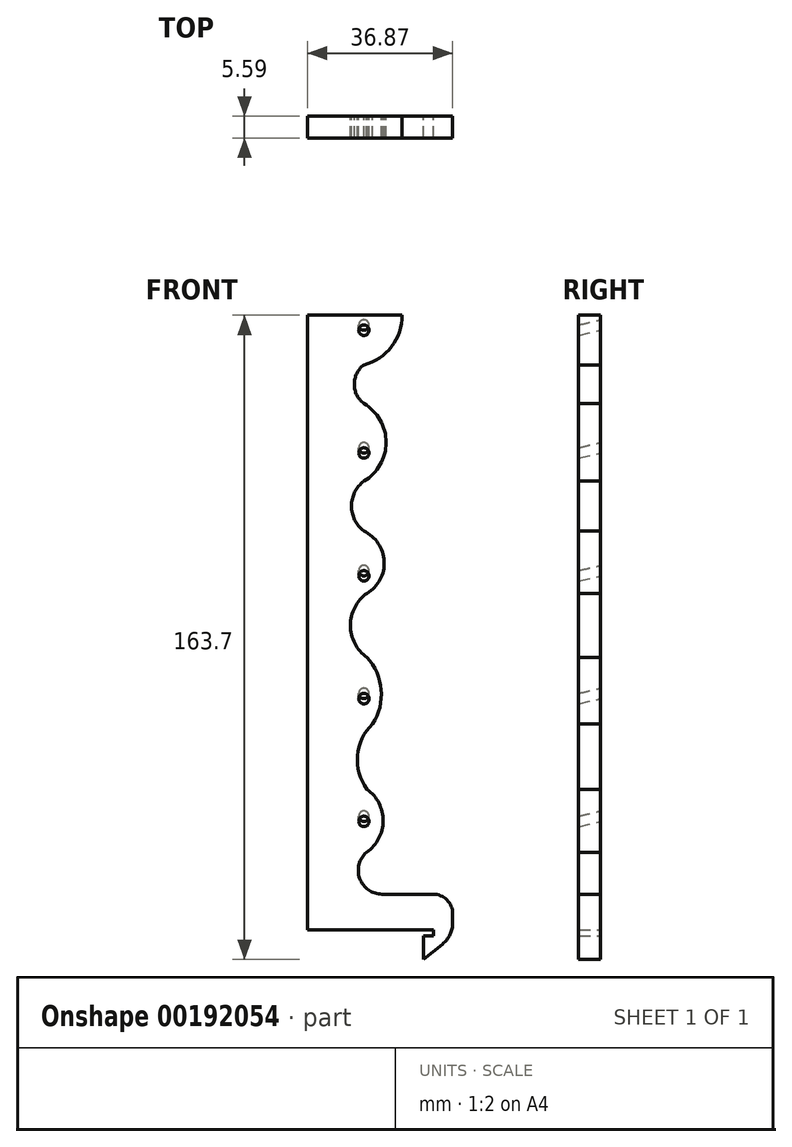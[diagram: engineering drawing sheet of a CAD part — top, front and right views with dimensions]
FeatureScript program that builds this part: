
annotation { "Feature Type Name" : "Feature", "Feature Type Description" : "" }
export const myFeature = defineFeature(function(context is Context, id is Id, definition is map)
    precondition{}
    {
        {
            var Q0;
            Q0=qCreatedBy(makeId("Front.planeOp"),FACE);
            var sketch = newSketch(context, id + "F0", { "sketchPlane" : qUnion([Q0])});
            skLineSegment(sketch, "E0", {"start": v(-18.93, 125.45) * mm, "end": v(-18.93, -30.75) * mm});
            skLineSegment(sketch, "E1", {"start": v(-18.93, 125.45) * mm, "end": v(5.07, 125.45) * mm});
            skLineSegment(sketch, "E2", {"start": v(10.57, -32.25) * mm, "end": v(13.07, -32.25) * mm});
            skLineSegment(sketch, "E3", {"start": v(-18.93, -30.75) * mm, "end": v(13.07, -30.75) * mm});
            skLineSegment(sketch, "E4", {"start": v(13.07, -32.25) * mm, "end": v(13.07, -30.75) * mm});
            skLineSegment(sketch, "E5", {"start": v(10.57, -32.25) * mm, "end": v(10.57, -38.25) * mm});
            skLineSegment(sketch, "E6", {"start": v(10.57, -38.25) * mm, "end": v(17.94, -32.25) * mm});
            skLineSegment(sketch, "E7", {"start": v(17.94, -32.25) * mm, "end": v(17.94, -21.65) * mm});
            skLineSegment(sketch, "E8", {"start": v(17.94, -21.65) * mm, "end": v(0, -21.65) * mm});
            skArc(sketch, "E9", {"start": v(-3.82, 54.79) * mm, "mid": v(-8.04, 46.64) * mm, "end": v(-3.82, 38.5) * mm});
            skArc(sketch, "E10", {"start": v(-2.38, 21.6) * mm, "mid": v(-0.24, 30.3) * mm, "end": v(-3.82, 38.5) * mm});
            skArc(sketch, "E11", {"start": v(-3.93, -11.02) * mm, "mid": v(0.26, -3.05) * mm, "end": v(-3.82, 4.98) * mm});
            skArc(sketch, "E12", {"start": v(-2.38, 21.6) * mm, "mid": v(-6.24, 13.56) * mm, "end": v(-3.82, 4.98) * mm});
            skLineSegment(sketch, "E13", {"start": v(-26.93, -1.85) * mm, "end": v(23.1, -1.85) * mm, "construction": true});
            skLineSegment(sketch, "E14", {"start": v(-26.93, 29.35) * mm, "end": v(26.02, 29.35) * mm, "construction": true});
            skLineSegment(sketch, "E15", {"start": v(-30.76, 60.55) * mm, "end": v(30.76, 60.55) * mm, "construction": true});
            skLineSegment(sketch, "E16", {"start": v(-31.73, 91.75) * mm, "end": v(30.5, 91.75) * mm, "construction": true});
            skLineSegment(sketch, "E17", {"start": v(-32.15, 122.95) * mm, "end": v(30.72, 122.95) * mm, "construction": true});
            skLineSegment(sketch, "E18", {"start": v(-4.63, -36.6) * mm, "end": v(-4.63, 141.82) * mm, "construction": true});
            skArc(sketch, "E19", {"start": v(-3.82, 54.79) * mm, "mid": v(0.54, 62.93) * mm, "end": v(-4.63, 70.6) * mm});
            skArc(sketch, "E20", {"start": v(-4.63, 83.29) * mm, "mid": v(-7.77, 76.94) * mm, "end": v(-4.63, 70.6) * mm});
            skArc(sketch, "E21", {"start": v(-4.63, 83.29) * mm, "mid": v(1.03, 93.13) * mm, "end": v(-4.63, 102.97) * mm});
            skArc(sketch, "E22", {"start": v(-4.63, 112.81) * mm, "mid": v(-7.06, 107.9) * mm, "end": v(-4.63, 102.97) * mm});
            skArc(sketch, "E23", {"start": v(-4.63, 112.81) * mm, "mid": v(2.4, 117.46) * mm, "end": v(5.07, 125.45) * mm});
            skArc(sketch, "E24", {"start": v(-3.93, -11.02) * mm, "mid": v(-5.67, -17.7) * mm, "end": v(0, -21.65) * mm});
            skSolve(sketch);
        }
        {
            var Q0;
            Q0=sQuery(id+"F0.wireOp",EDGE,"E13");
            cPlane(context, id + "F1", {"entities" : qUnion([Q0]), "cplaneType" : CPlaneType.LINE_ANGLE, "offset" : 25 * mm, "angle" : 13.27 * degree, "width" : 150 * mm, "height" : 150 * mm});
        }
        {
            var Q0;
            Q0=sQuery(id+"F0.wireOp",EDGE,"E14");
            cPlane(context, id + "F2", {"entities" : qUnion([Q0]), "cplaneType" : CPlaneType.LINE_ANGLE, "offset" : 25 * mm, "angle" : 13.27 * degree, "width" : 150 * mm, "height" : 150 * mm});
        }
        {
            var Q0;
            Q0=sQuery(id+"F0.wireOp",EDGE,"E15");
            cPlane(context, id + "F3", {"entities" : qUnion([Q0]), "cplaneType" : CPlaneType.LINE_ANGLE, "offset" : 25 * mm, "angle" : 13.27 * degree, "width" : 150 * mm, "height" : 150 * mm});
        }
        {
            var Q0;
            Q0=qCreatedBy(id+"F1.planeOp",FACE);
            var sketch = newSketch(context, id + "F4", { "sketchPlane" : qUnion([Q0])});
            skCircle(sketch, "E25", {"center": v(4.63, -1.8) * mm, "radius": 1.3 * mm});
            skSolve(sketch);
        }
        {
            var Q0;
            Q0=qCreatedBy(id+"F2.planeOp",FACE);
            var sketch = newSketch(context, id + "F5", { "sketchPlane" : qUnion([Q0])});
            skCircle(sketch, "E26", {"center": v(4.63, 28.56) * mm, "radius": 1.3 * mm});
            skSolve(sketch);
        }
        {
            var Q0;
            Q0=qCreatedBy(id+"F3.planeOp",FACE);
            var sketch = newSketch(context, id + "F6", { "sketchPlane" : qUnion([Q0])});
            skCircle(sketch, "E27", {"center": v(4.63, 58.93) * mm, "radius": 1.3 * mm});
            skSolve(sketch);
        }
        {
            var Q0;
            Q0=sQuery(id+"F0.wireOp",EDGE,"E16");
            cPlane(context, id + "F7", {"entities" : qUnion([Q0]), "cplaneType" : CPlaneType.LINE_ANGLE, "offset" : 25 * mm, "angle" : 13.27 * degree, "width" : 150 * mm, "height" : 150 * mm});
        }
        {
            var Q0;
            Q0=sQuery(id+"F0.wireOp",EDGE,"E17");
            cPlane(context, id + "F8", {"entities" : qUnion([Q0]), "cplaneType" : CPlaneType.LINE_ANGLE, "offset" : 25 * mm, "angle" : 13.27 * degree, "width" : 150 * mm, "height" : 150 * mm});
        }
        {
            var Q0;
            Q0=qCreatedBy(id+"F7.planeOp",FACE);
            var sketch = newSketch(context, id + "F9", { "sketchPlane" : qUnion([Q0])});
            skCircle(sketch, "E28", {"center": v(4.63, 89.3) * mm, "radius": 1.3 * mm});
            skSolve(sketch);
        }
        {
            var Q0;
            Q0=qCreatedBy(id+"F8.planeOp",FACE);
            var sketch = newSketch(context, id + "F10", { "sketchPlane" : qUnion([Q0])});
            skCircle(sketch, "E29", {"center": v(4.63, 119.66) * mm, "radius": 1.3 * mm});
            skSolve(sketch);
        }
        {
            var Q0;
            Q0=makeQuery(id+"F0.imprint","IMPRINT",FACE,{"disambiguationData":[TD([[makeQuery(id+"F0.imprint","IMPRINT",EDGE,{"derivedFrom":sQuery(id+"F0.wireOp",EDGE,"E0")}),1.0]])]});
            extrude(context, id + "F11", {"entities" : qUnion([Q0]), "depth" : 5.6 * mm});
        }
        {
            var Q0;
            Q0 = qSketchRegion(id + "F4", true);
            var Q1;
            Q1 = qSketchRegion(id + "F5", true);
            var Q2;
            Q2 = qSketchRegion(id + "F9", true);
            var Q3;
            Q3 = qSketchRegion(id + "F6", true);
            var Q4;
            Q4 = qSketchRegion(id + "F10", true);
            extrude(context, id + "F12", {"entities" : qUnion([Q0, Q1, Q2, Q3, Q4]), "operationType" : NewBodyOperationType.REMOVE, "endBound" : BoundingType.SYMMETRIC, "oppositeDirection" : true, "depth" : 25 * mm});
        }
        {
            var Q0;
            Q0=makeQuery(id+"F11.opExtrude","SWEPT_EDGE",EDGE,{"disambiguationData":[OSD([sQuery(id+"F0.wireOp",EDGE,"E7"),sQuery(id+"F0.wireOp",EDGE,"E8")])]});
            fillet(context, id + "F13", {"entities" : qUnion([Q0]), "radius" : 5 * mm, "tangentPropagation" : true, "allowEdgeOverflow" : false});
        }
        {
            var Q0;
            Q0=makeQuery(id+"F11.opExtrude","SWEPT_EDGE",EDGE,{"disambiguationData":[OSD([sQuery(id+"F0.wireOp",EDGE,"E6"),sQuery(id+"F0.wireOp",EDGE,"E7")])]});
            fillet(context, id + "F14", {"entities" : qUnion([Q0]), "radius" : 7 * mm, "tangentPropagation" : true, "allowEdgeOverflow" : false});
        }
    });
